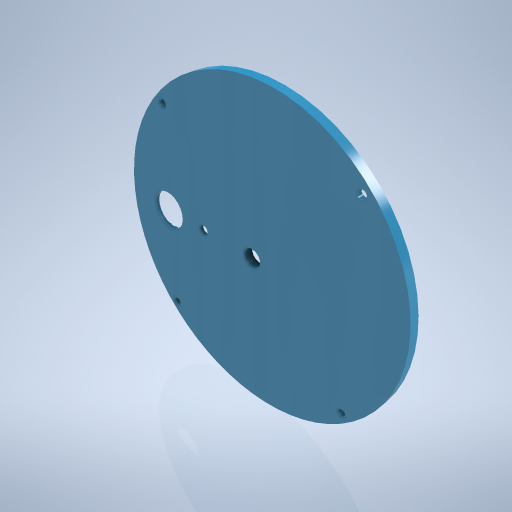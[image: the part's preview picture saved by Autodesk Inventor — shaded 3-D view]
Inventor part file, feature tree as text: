
AUTODESK INVENTOR PART (.ipt)
format: ipt  version: 2024.2 (Build 282272000, 272)  size: 498,688 bytes
history: native  units: mm
features: sketch x6, hole x4, revolve x1, plane x1, extrude x1, fillet x1, pattern_circular x1
ambient origin geometry x8: Origin, YZ Plane, XZ Plane, XY Plane, X Axis, Y Axis, Z Axis, Center Point
bodies: Volumenkörper1 (feature_tree)
feature tree (15):
  revolve  "Umdrehung1"
  plane  "Arbeitsebene1"
  extrude  "Extrusion3"  TaperAngle=60.0deg  [1 undecoded]
  fillet  "Rundung1"  Radius=3.0mm
  hole  "Bohrung3"  [1 undecoded]
  hole  "Bohrung4"  [1 undecoded]
  pattern_circular  "Runde Anordnung2"  Count=2  [1 undecoded]
  hole  "Bohrung5"  [1 undecoded]
  hole  "Bohrung6"  [1 undecoded]
  sketch  "Skizze1"  dims[d0=15.0mm d2=60.0deg d3=3.0mm]
  sketch  "Skizze6"  dims[d4=2.0mm d5=90.0mm d7=3.0mm d8=10.0mm d10=10.0mm]
  sketch  "Skizze7"  dims[d12=3.0mm d13=100.0mm d14=20.0mm]
  sketch  "Skizze8"  dims[d15=90.0deg]
  sketch  "Skizze9"  dims[d42=6.0mm d43=6.0mm d44=4.0mm d45=2.0mm d46=90.0deg d47=8.0mm d48=0.0mm d50=0.5mm]
  sketch  "Skizze10"  dims[d56=-1.8mm d58=11.8mm d59=15.0mm d60=10.0mm d61=0.0mm d62=2.0mm d63=2.7mm d64=6.0mm d65=5.5mm d66=2.0mm d67=90.0deg d68=8.0mm d69=20.594885mm d70=45.0deg d71=47.0mm d72=40.0mm d73=360.0deg d75=12.0mm d76=6.0mm d77=5.5mm d78=2.0mm d79=90.0deg d80=8.0mm d81=0.0mm d82=34.0mm d83=3.2mm d84=6.0mm d85=4.0mm d86=2.0mm d87=90.0deg d88=8.0mm d89=0.0mm d90=19.0mm d91=1.0mm d92=1.0mm d93=1.0mm d94=0.15mm d95=0.25mm d96=0.375mm d97=14.3117mm d98=0.75mm d99=20.594885mm d100=0.0625mm d101=0.75mm d102=0.375mm]
note: 6 required parameter values undecoded (feature->parameter linkage not recoverable at this tier; creation-order binding heuristic only, values carry confidence <= 0.55)
